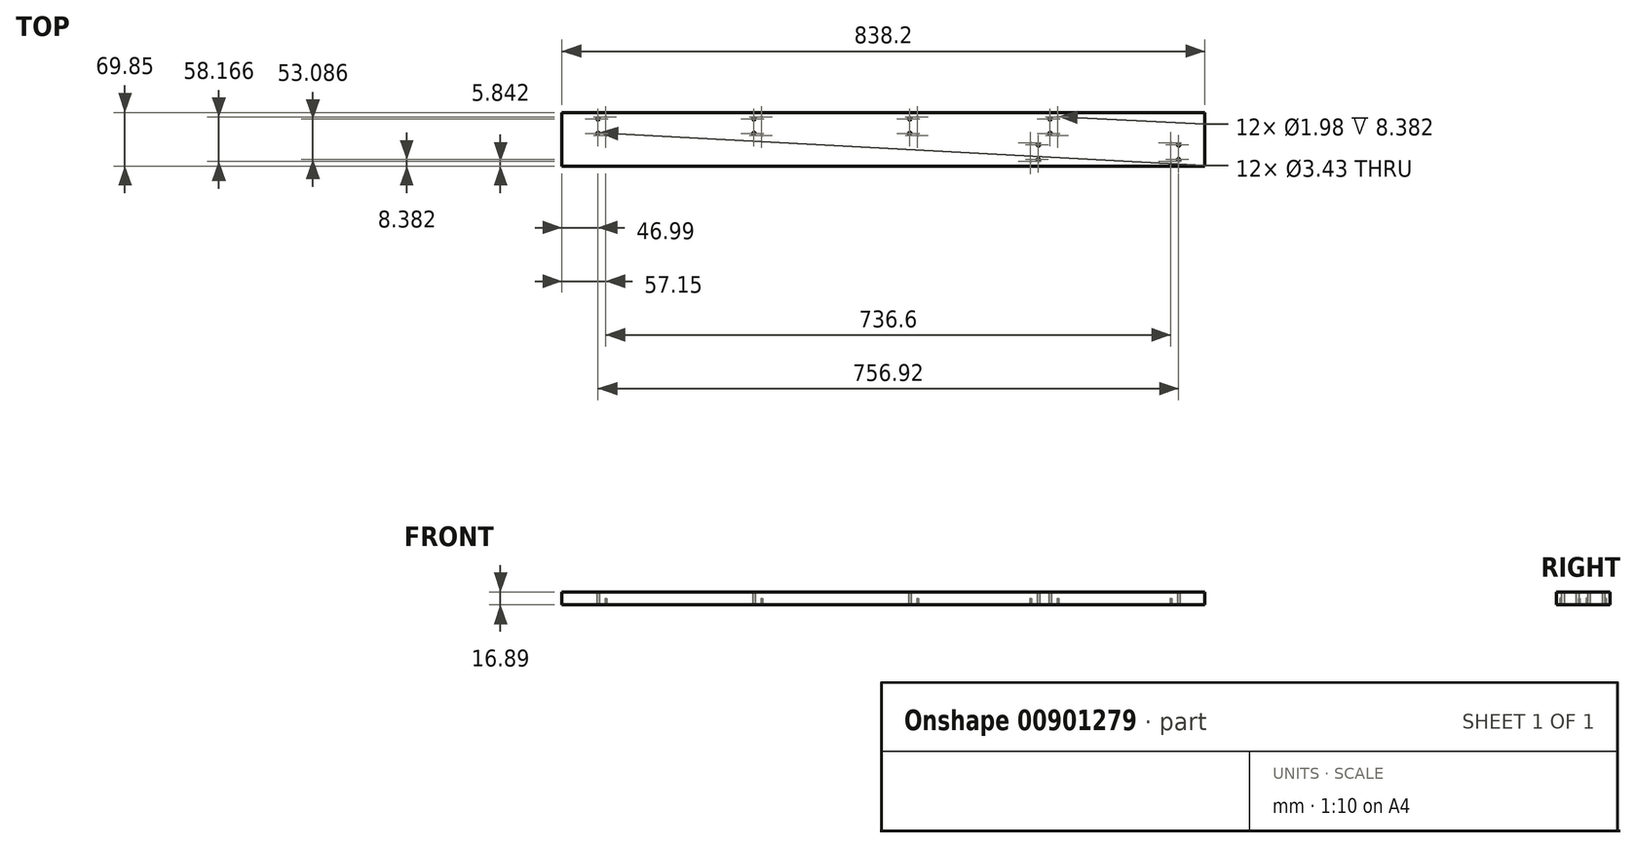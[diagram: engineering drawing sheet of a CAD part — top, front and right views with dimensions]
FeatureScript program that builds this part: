
annotation { "Feature Type Name" : "Feature", "Feature Type Description" : "" }
export const myFeature = defineFeature(function(context is Context, id is Id, definition is map)
    precondition{}
    {
        {
            var Q0;
            Q0=qCreatedBy(makeId("Top.planeOp"),FACE);
            var sketch = newSketch(context, id + "F0", { "sketchPlane" : qUnion([Q0])});
            skLineSegment(sketch, "E0.bottom", {"start": v(0, 0) * mm, "end": v(838.2, 0) * mm});
            skLineSegment(sketch, "E0.top", {"start": v(0, 69.85) * mm, "end": v(838.2, 69.85) * mm});
            skLineSegment(sketch, "E0.left", {"start": v(0, 0) * mm, "end": v(0, 69.85) * mm});
            skLineSegment(sketch, "E0.right", {"start": v(838.2, 0) * mm, "end": v(838.2, 69.85) * mm});
            skSolve(sketch);
        }
        {
            var Q0;
            Q0 = qSketchRegion(id + "F0", true);
            extrude(context, id + "F1", {"entities" : qUnion([Q0]), "depth" : 16.9 * mm, "offsetDistance" : 25.4 * mm});
        }
        {
            var Q0;
            Q0=makeQuery(id+"F1.opExtrude","CAP_FACE",FACE,{"disambiguationData":[OSD([sQuery(id+"F0.wireOp",EDGE,"E0.bottom"),sQuery(id+"F0.wireOp",EDGE,"E0.top"),sQuery(id+"F0.wireOp",EDGE,"E0.left"),sQuery(id+"F0.wireOp",EDGE,"E0.right")])],"isStart":true});
            var sketch = newSketch(context, id + "F2", { "sketchPlane" : qUnion([Q0])});
            skCircle(sketch, "E1", {"center": v(793.75, -5.84) * mm, "radius": 1 * mm});
            skCircle(sketch, "E2", {"center": v(793.75, -29.97) * mm, "radius": 1 * mm});
            skCircle(sketch, "E3", {"center": v(646.43, -39.88) * mm, "radius": 1 * mm});
            skCircle(sketch, "E4", {"center": v(646.43, -64) * mm, "radius": 1 * mm});
            skCircle(sketch, "E5.1.0.0", {"center": v(463.55, -64) * mm, "radius": 1 * mm});
            skCircle(sketch, "E5.1.0.1", {"center": v(610.87, -29.97) * mm, "radius": 1 * mm});
            skCircle(sketch, "E5.1.0.2", {"center": v(463.55, -39.88) * mm, "radius": 1 * mm});
            skCircle(sketch, "E5.1.0.3", {"center": v(610.87, -5.84) * mm, "radius": 1 * mm});
            skLineSegment(sketch, "E5.direction1", {"start": v(646.43, -64) * mm, "end": v(463.55, -64) * mm, "construction": true});
            skCircle(sketch, "E6.1.0.0", {"center": v(260.35, -39.88) * mm, "radius": 1 * mm});
            skCircle(sketch, "E6.1.0.1", {"center": v(260.35, -64) * mm, "radius": 1 * mm});
            skCircle(sketch, "E6.2.0.0", {"center": v(57.15, -39.88) * mm, "radius": 1 * mm});
            skCircle(sketch, "E6.2.0.1", {"center": v(57.15, -64) * mm, "radius": 1 * mm});
            skLineSegment(sketch, "E6.direction1", {"start": v(463.55, -64) * mm, "end": v(260.35, -64) * mm, "construction": true});
            skSolve(sketch);
        }
        {
            var Q0;
            Q0 = qSketchRegion(id + "F2", true);
            extrude(context, id + "F3", {"entities" : qUnion([Q0]), "operationType" : NewBodyOperationType.REMOVE, "oppositeDirection" : true, "depth" : 8.38 * mm, "offsetDistance" : 25.4 * mm});
        }
        {
            var Q0;
            Q0=makeQuery(id+"F1.opExtrude","CAP_FACE",FACE,{"disambiguationData":[OSD([sQuery(id+"F0.wireOp",EDGE,"E0.bottom"),sQuery(id+"F0.wireOp",EDGE,"E0.top"),sQuery(id+"F0.wireOp",EDGE,"E0.left"),sQuery(id+"F0.wireOp",EDGE,"E0.right")])],"isStart":true});
            var sketch = newSketch(context, id + "F4", { "sketchPlane" : qUnion([Q0])});
            skPoint(sketch, "E7", {"position": v(793.75, -5.84) * mm});
            skPoint(sketch, "E8", {"position": v(793.75, -29.97) * mm});
            skPoint(sketch, "E9", {"position": v(646.43, -39.88) * mm});
            skPoint(sketch, "E10", {"position": v(646.43, -64) * mm});
            skCircle(sketch, "E11", {"center": v(803.91, -8.38) * mm, "radius": 1.71 * mm});
            skCircle(sketch, "E12", {"center": v(803.91, -27.43) * mm, "radius": 1.71 * mm});
            skCircle(sketch, "E13", {"center": v(636.27, -42.42) * mm, "radius": 1.71 * mm});
            skCircle(sketch, "E14", {"center": v(636.27, -61.47) * mm, "radius": 1.71 * mm});
            skPoint(sketch, "E15.1.0.0", {"position": v(463.55, -39.88) * mm});
            skCircle(sketch, "E15.1.0.1", {"center": v(453.4, -42.42) * mm, "radius": 1.71 * mm});
            skPoint(sketch, "E15.1.0.2", {"position": v(610.87, -5.84) * mm});
            skCircle(sketch, "E15.1.0.3", {"center": v(453.4, -61.47) * mm, "radius": 1.71 * mm});
            skPoint(sketch, "E15.1.0.4", {"position": v(463.55, -64) * mm});
            skPoint(sketch, "E15.1.0.5", {"position": v(610.87, -29.97) * mm});
            skCircle(sketch, "E15.1.0.6", {"center": v(621.03, -27.43) * mm, "radius": 1.71 * mm});
            skCircle(sketch, "E15.1.0.7", {"center": v(621.03, -8.38) * mm, "radius": 1.71 * mm});
            skLineSegment(sketch, "E15.direction1", {"start": v(646.43, -64) * mm, "end": v(463.55, -64) * mm, "construction": true});
            skPoint(sketch, "E16.1.0.0", {"position": v(260.35, -64) * mm});
            skPoint(sketch, "E16.1.0.1", {"position": v(260.35, -39.88) * mm});
            skCircle(sketch, "E16.1.0.2", {"center": v(250.2, -42.42) * mm, "radius": 1.71 * mm});
            skCircle(sketch, "E16.1.0.3", {"center": v(250.2, -61.47) * mm, "radius": 1.71 * mm});
            skPoint(sketch, "E16.2.0.0", {"position": v(57.15, -64) * mm});
            skPoint(sketch, "E16.2.0.1", {"position": v(57.15, -39.88) * mm});
            skCircle(sketch, "E16.2.0.2", {"center": v(47, -42.42) * mm, "radius": 1.71 * mm});
            skCircle(sketch, "E16.2.0.3", {"center": v(47, -61.47) * mm, "radius": 1.71 * mm});
            skLineSegment(sketch, "E16.direction1", {"start": v(463.55, -64) * mm, "end": v(260.35, -64) * mm, "construction": true});
            skSolve(sketch);
        }
        {
            var Q0;
            Q0 = qSketchRegion(id + "F4", true);
            extrude(context, id + "F5", {"entities" : qUnion([Q0]), "operationType" : NewBodyOperationType.REMOVE, "oppositeDirection" : true, "depth" : 25.4 * mm, "offsetDistance" : 25.4 * mm});
        }
    });
